# Revit family: FU_Chair_Sandler_Woodlook 2-8C
name_source: partatom
category: Furniture
units: mm (PartAtom-declared; Revit-internal decimal feet)

## family parameters
Always vertical = Yes
Cut with Voids When Loaded = No
OmniClass Number = 23.40.20.00
OmniClass Title = General Furniture and Specialties
Room Calculation Point = No
Shared = No
Work Plane-Based = No

## types (1)
- FU_Chair_Sandler_Woodlook 2-8C
    D = 592 mm  [stored 1.94226 ft]
    Default Elevation = 0 mm  [stored 0 ft]
    Description = Woodlook armchair with frame manufactured entirely from aluminum but with realistic appearance of wood. With casters in nylon (suitable for carpet floors) or polyurethane (suitable for wood or tile floors). Highly durable and scratch resistant.
    H = 965 mm  [stored 3.16601 ft]
    Manufacturer = Sandler
    Model = Woodlook 2.8C
    URL = https://www.sandlerseating.com
    Upholstery = Fabric - Gravity - Frost CPC32
    W = 610 mm  [stored 2.00131 ft]
    Woodlook = Woodlook - 21A Teak

note: [stored X ft] marks values corroborated as IEEE doubles in the binary element streams (Revit-internal decimal feet)

## geometry (parser evidence)
native form markers: Sweep x9
no freeform markers — native parametric forms only
